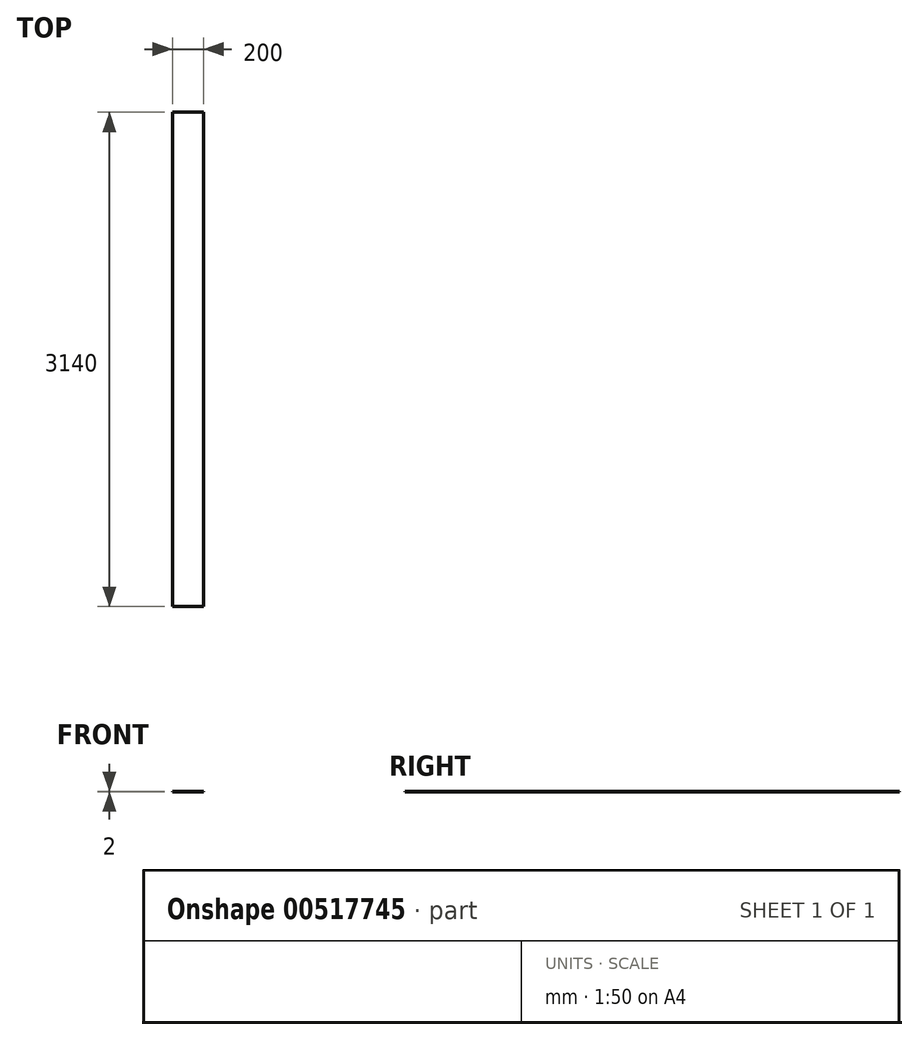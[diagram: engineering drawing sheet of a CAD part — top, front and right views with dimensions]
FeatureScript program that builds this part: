
annotation { "Feature Type Name" : "Feature", "Feature Type Description" : "" }
export const myFeature = defineFeature(function(context is Context, id is Id, definition is map)
    precondition{}
    {
        {
            var Q0;
            Q0=qCreatedBy(makeId("Top.planeOp"),FACE);
            var sketch = newSketch(context, id + "F0", { "sketchPlane" : qUnion([Q0])});
            skLineSegment(sketch, "E0.bottom", {"start": v(0, 0) * mm, "end": v(200, 0) * mm});
            skLineSegment(sketch, "E0.top", {"start": v(0, 3140) * mm, "end": v(200, 3140) * mm});
            skLineSegment(sketch, "E0.left", {"start": v(0, 0) * mm, "end": v(0, 3140) * mm});
            skLineSegment(sketch, "E0.right", {"start": v(200, 0) * mm, "end": v(200, 3140) * mm});
            skSolve(sketch);
        }
        {
            var Q0;
            Q0 = qSketchRegion(id + "F0", true);
            extrude(context, id + "F1", {"entities" : qUnion([Q0]), "depth" : 2 * mm, "offsetDistance" : 25 * mm});
        }
    });
